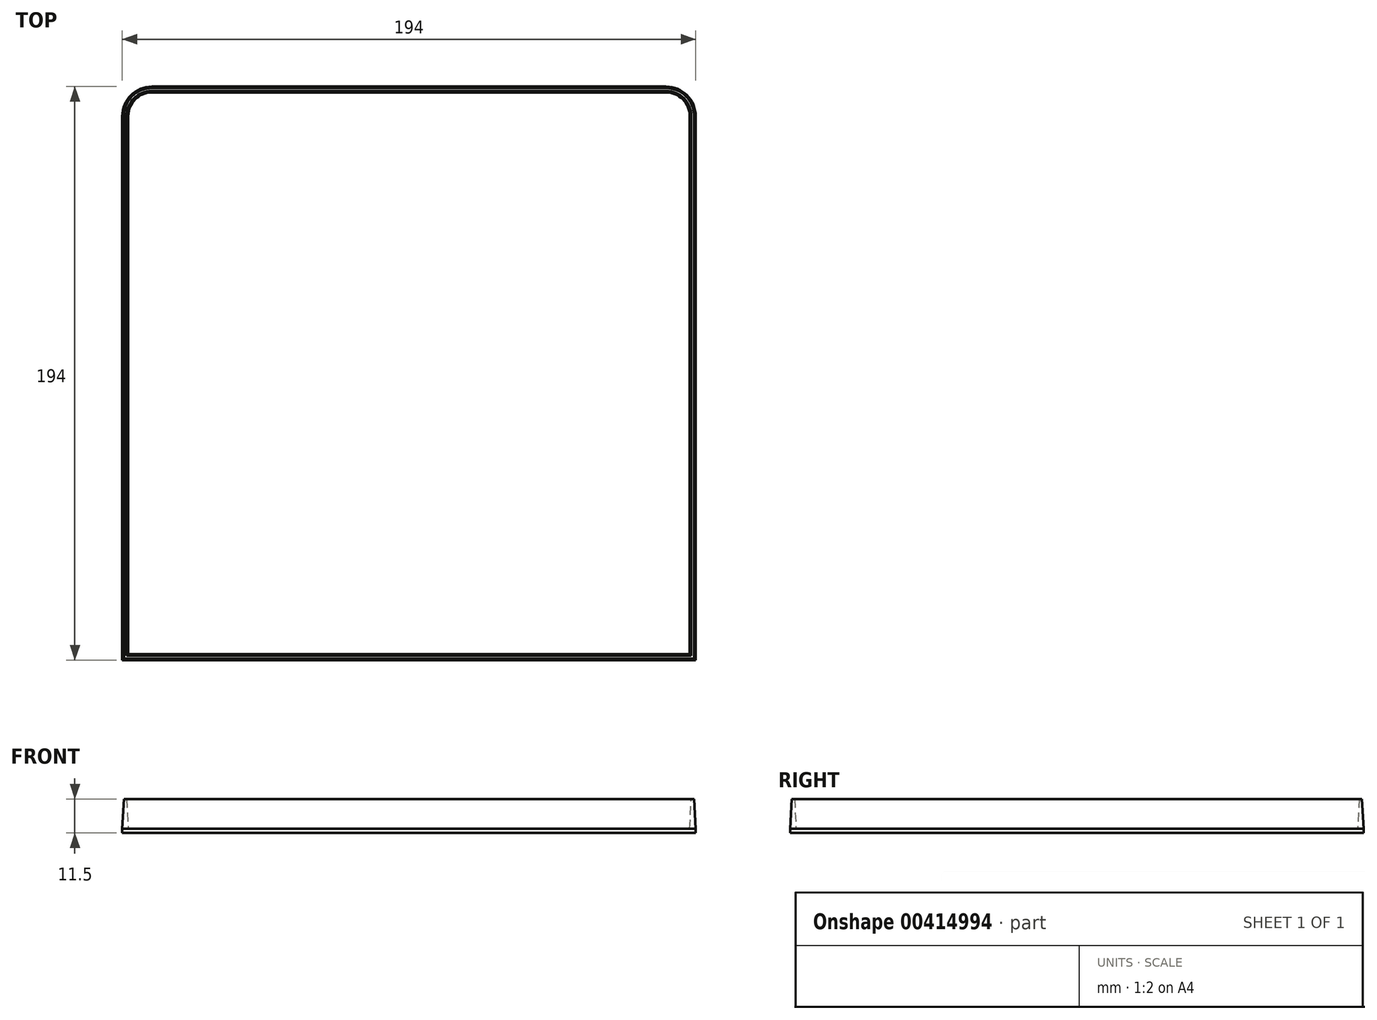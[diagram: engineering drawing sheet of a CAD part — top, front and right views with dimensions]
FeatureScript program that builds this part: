
annotation { "Feature Type Name" : "Feature", "Feature Type Description" : "" }
export const myFeature = defineFeature(function(context is Context, id is Id, definition is map)
    precondition{}
    {
        {
            var Q0;
            Q0=qCreatedBy(makeId("Top.planeOp"),FACE);
            var sketch = newSketch(context, id + "F0", { "sketchPlane" : qUnion([Q0])});
            skLineSegment(sketch, "E0.bottom", {"start": v(97, -97) * mm, "end": v(-97, -97) * mm});
            skLineSegment(sketch, "E0.top", {"start": v(87, 97) * mm, "end": v(-87, 97) * mm});
            skLineSegment(sketch, "E0.left", {"start": v(97, -97) * mm, "end": v(97, 87) * mm});
            skLineSegment(sketch, "E0.right", {"start": v(-97, -97) * mm, "end": v(-97, 87) * mm});
            skPoint(sketch, "E0.middle", {"position": v(0, 0) * mm});
            skPoint(sketch, "E1.visualSharp", {"position": v(-97, 97) * mm});
            skArc(sketch, "E1.filletArc", {"start": v(-87, 97) * mm, "mid": v(-94.07, 94.07) * mm, "end": v(-97, 87) * mm});
            skPoint(sketch, "E2.visualSharp", {"position": v(97, 97) * mm});
            skArc(sketch, "E2.filletArc", {"start": v(97, 87) * mm, "mid": v(94.07, 94.07) * mm, "end": v(87, 97) * mm});
            skLineSegment(sketch, "E3.0", {"start": v(95, -95) * mm, "end": v(-95, -95) * mm});
            skArc(sketch, "E3.1", {"start": v(-87, 95) * mm, "mid": v(-92.66, 92.66) * mm, "end": v(-95, 87) * mm});
            skLineSegment(sketch, "E3.2", {"start": v(87, 95) * mm, "end": v(-87, 95) * mm});
            skLineSegment(sketch, "E3.3", {"start": v(-95, -95) * mm, "end": v(-95, 87) * mm});
            skArc(sketch, "E3.4", {"start": v(95, 87) * mm, "mid": v(92.66, 92.66) * mm, "end": v(87, 95) * mm});
            skLineSegment(sketch, "E3.5", {"start": v(95, -95) * mm, "end": v(95, 87) * mm});
            skSolve(sketch);
        }
        {
            var Q0;
            Q0 = qSketchRegion(id + "F0", true);
            extrude(context, id + "F1", {"entities" : qUnion([Q0]), "depth" : 10 * mm, "offsetDistance" : 25.4 * mm, "hasDraft" : true, "draftAngle" : 3 * degree, "draftPullDirection" : true});
        }
        {
            var Q0;
            Q0=makeQuery(id+"F1.opExtrude","CAP_FACE",FACE,{"disambiguationData":[OSD([sQuery(id+"F0.wireOp",EDGE,"E0.bottom"),sQuery(id+"F0.wireOp",EDGE,"E0.top"),sQuery(id+"F0.wireOp",EDGE,"E0.left"),sQuery(id+"F0.wireOp",EDGE,"E0.right"),sQuery(id+"F0.wireOp",EDGE,"E1.filletArc"),sQuery(id+"F0.wireOp",EDGE,"E2.filletArc"),sQuery(id+"F0.wireOp",EDGE,"E3.0"),sQuery(id+"F0.wireOp",EDGE,"E3.1"),sQuery(id+"F0.wireOp",EDGE,"E3.2"),sQuery(id+"F0.wireOp",EDGE,"E3.3"),sQuery(id+"F0.wireOp",EDGE,"E3.4"),sQuery(id+"F0.wireOp",EDGE,"E3.5")])],"isStart":true});
            var sketch = newSketch(context, id + "F2", { "sketchPlane" : qUnion([Q0])});
            skLineSegment(sketch, "E4.0", {"start": v(97, 97) * mm, "end": v(-97, 97) * mm});
            skLineSegment(sketch, "E5.0", {"start": v(-97, 97) * mm, "end": v(-97, -87) * mm});
            skArc(sketch, "E6.0", {"start": v(-87, -97) * mm, "mid": v(-94.07, -94.07) * mm, "end": v(-97, -87) * mm});
            skLineSegment(sketch, "E7.0", {"start": v(87, -97) * mm, "end": v(-87, -97) * mm});
            skArc(sketch, "E8.0", {"start": v(97, -87) * mm, "mid": v(94.07, -94.07) * mm, "end": v(87, -97) * mm});
            skLineSegment(sketch, "E9.0", {"start": v(97, 97) * mm, "end": v(97, -87) * mm});
            skSolve(sketch);
        }
        {
            var Q0;
            Q0 = qSketchRegion(id + "F2", true);
            extrude(context, id + "F3", {"entities" : qUnion([Q0]), "operationType" : NewBodyOperationType.ADD, "depth" : 1.5 * mm, "offsetDistance" : 25.4 * mm});
        }
    });
